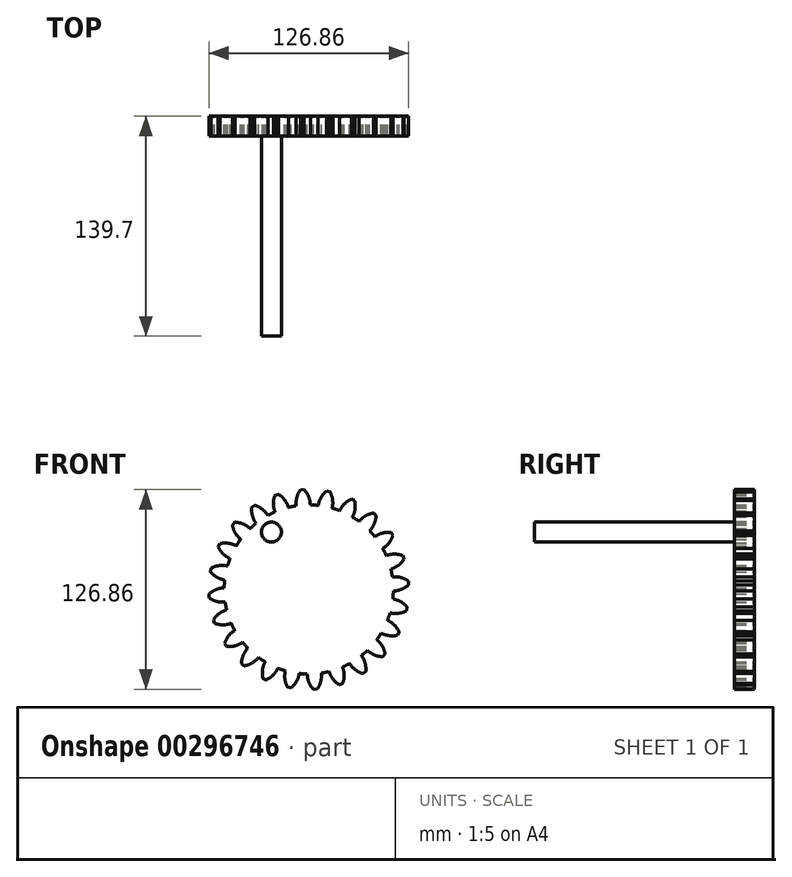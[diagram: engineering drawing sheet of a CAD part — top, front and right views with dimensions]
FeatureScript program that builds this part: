
annotation { "Feature Type Name" : "Feature", "Feature Type Description" : "" }
export const myFeature = defineFeature(function(context is Context, id is Id, definition is map)
    precondition{}
    {
        {
            var Q0;
            Q0=qCreatedBy(makeId("Front.planeOp"),FACE);
            var sketch = newSketch(context, id + "F0", { "sketchPlane" : qUnion([Q0])});
            skCircle(sketch, "E0", {"center": v(0, 0) * mm, "radius": 58.67 * mm, "construction": true});
            skCircle(sketch, "E1", {"center": v(0, 0) * mm, "radius": 63.5 * mm, "construction": true});
            skCircle(sketch, "E2", {"center": v(0, 0) * mm, "radius": 53.72 * mm});
            skLineSegment(sketch, "E3", {"start": v(0, 0) * mm, "end": v(0, 83.58) * mm, "construction": true});
            skLineSegment(sketch, "E4", {"start": v(0, 0) * mm, "end": v(-5.45, 83.17) * mm, "construction": true});
            skLineSegment(sketch, "E5", {"start": v(0, 58.67) * mm, "end": v(-81.86, 58.67) * mm, "construction": true});
            skLineSegment(sketch, "E6", {"start": v(-81.86, 58.67) * mm, "end": v(0, 58.67) * mm, "construction": true});
            skLineSegment(sketch, "E7", {"start": v(0, 58.67) * mm, "end": v(-77.07, 30.62) * mm, "construction": true});
            skCircle(sketch, "E8", {"center": v(0, 58.67) * mm, "radius": 14.6 * mm, "construction": true});
            skCircle(sketch, "E9", {"center": v(0, 0) * mm, "radius": 55.14 * mm, "construction": true});
            skCircle(sketch, "E10", {"center": v(-13.63, 53.42) * mm, "radius": 14.6 * mm, "construction": true});
            skArc(sketch, "E11", {"start": v(0, 58.67) * mm, "mid": v(-1.28, 61.19) * mm, "end": v(-2.99, 63.43) * mm});
            skArc(sketch, "E12", {"start": v(0.97, 53.71) * mm, "mid": v(0.72, 56.24) * mm, "end": v(0, 58.67) * mm});
            skArc(sketch, "E13.MirrorCS", {"start": v(-7.66, 58.17) * mm, "mid": v(-6.72, 60.83) * mm, "end": v(-5.32, 63.28) * mm});
            skArc(sketch, "E14.MirrorCS", {"start": v(-7.98, 53.13) * mm, "mid": v(-8.05, 55.66) * mm, "end": v(-7.66, 58.17) * mm});
            skLineSegment(sketch, "E15", {"start": v(-5.32, 63.28) * mm, "end": v(-2.99, 63.43) * mm});
            skSolve(sketch);
        }
        {
            var Q0;
            {var subQ0=sQuery(id+"F0.wireOp",EDGE,"E2");var subQ1=makeQuery(id+"F0.imprint","INTERSECT",VERTEX,{"derivedFrom":[subQ0,sQuery(id+"F0.wireOp",EDGE,"E12")]});Q0=makeQuery(id+"F0.imprint","IMPRINT",FACE,{"disambiguationData":[TD([[makeQuery(id+"F0.imprint","IMPRINT",EDGE,{"disambiguationData":[TD([[subQ1,-1.0]])],"derivedFrom":subQ0}),1.0]])]});}
            var Q1;
            Q1=makeQuery(id+"F0.imprint","IMPRINT",FACE,{"disambiguationData":[TD([[makeQuery(id+"F0.imprint","IMPRINT",EDGE,{"derivedFrom":sQuery(id+"F0.wireOp",EDGE,"E11")}),1.0]])]});
            extrude(context, id + "F1", {"entities" : qUnion([Q0, Q1]), "depth" : 12.7 * mm});
        }
        {
            var Q0;
            Q0=makeQuery(id+"F1.opExtrude","SWEPT_BODY",BODY,{"disambiguationData":[OSD([sQuery(id+"F0.wireOp",EDGE,"E2"),sQuery(id+"F0.wireOp",EDGE,"E11"),sQuery(id+"F0.wireOp",EDGE,"E12"),sQuery(id+"F0.wireOp",EDGE,"E13.MirrorCS"),sQuery(id+"F0.wireOp",EDGE,"E14.MirrorCS"),sQuery(id+"F0.wireOp",EDGE,"E15")])]});
            var Q1;
            Q1=makeQuery(id+"F1.opExtrude","SWEPT_FACE",FACE,{"disambiguationData":[OSD([sQuery(id+"F0.wireOp",EDGE,"E2")])]});
            circularPattern(context, id + "F2", {"entities" : qUnion([Q0]), "axis" : qUnion([Q1]), "angle" : 360 * degree, "instanceCount" : 24, "equalSpace" : true});
        }
        {
            var Q0;
            Q0=makeQuery(id+"F1.opExtrude","CAP_FACE",FACE,{"disambiguationData":[OSD([sQuery(id+"F0.wireOp",EDGE,"E2"),sQuery(id+"F0.wireOp",EDGE,"E11"),sQuery(id+"F0.wireOp",EDGE,"E12"),sQuery(id+"F0.wireOp",EDGE,"E13.MirrorCS"),sQuery(id+"F0.wireOp",EDGE,"E14.MirrorCS"),sQuery(id+"F0.wireOp",EDGE,"E15")])],"isStart":false});
            var sketch = newSketch(context, id + "F3", { "sketchPlane" : qUnion([Q0])});
            skCircle(sketch, "E16", {"center": v(-23.73, 36.44) * mm, "radius": 6.35 * mm});
            skSolve(sketch);
        }
        {
            var Q0;
            Q0=makeQuery(id+"F3.imprint","IMPRINT",FACE,{"disambiguationData":[TD([[makeQuery(id+"F3.imprint","IMPRINT",EDGE,{"derivedFrom":sQuery(id+"F3.wireOp",EDGE,"E16")}),1.0]])]});
            extrude(context, id + "F4", {"entities" : qUnion([Q0]), "operationType" : NewBodyOperationType.ADD, "depth" : 127 * mm});
        }
    });
